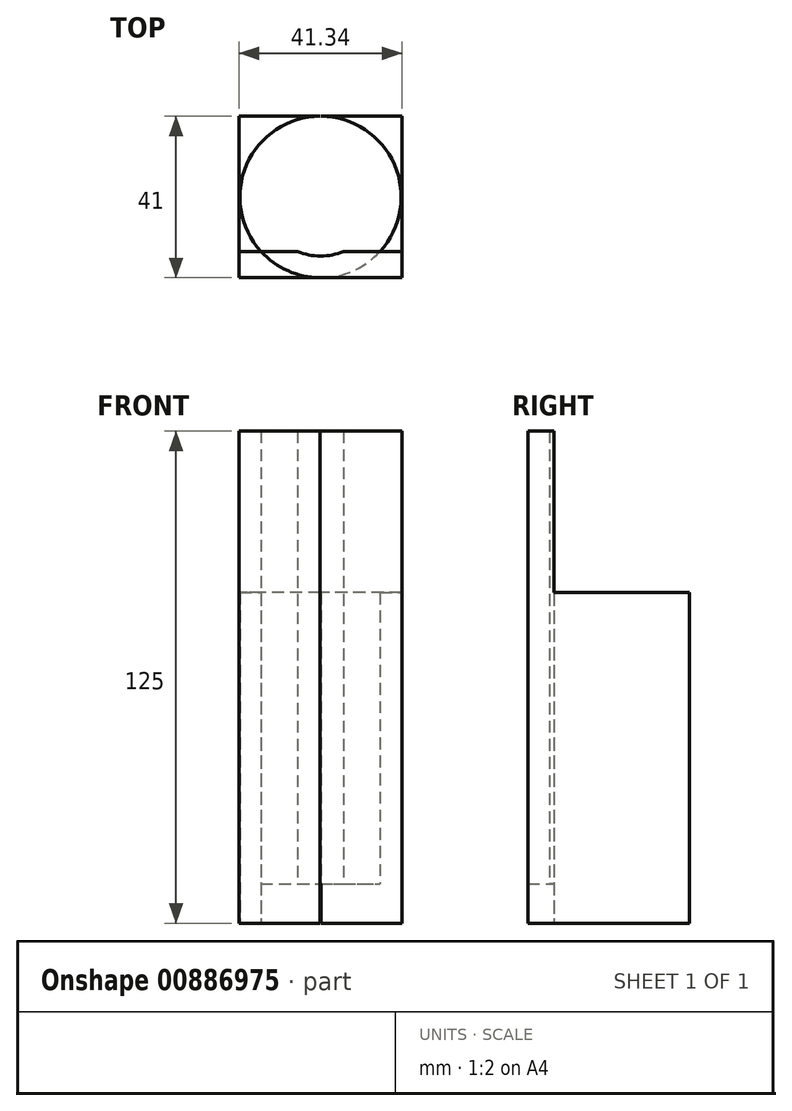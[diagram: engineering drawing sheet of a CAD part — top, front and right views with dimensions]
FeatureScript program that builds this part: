
annotation { "Feature Type Name" : "Feature", "Feature Type Description" : "" }
export const myFeature = defineFeature(function(context is Context, id is Id, definition is map)
    precondition{}
    {
        {
            var Q0;
            Q0=qCreatedBy(makeId("Top.planeOp"),FACE);
            var sketch = newSketch(context, id + "F0", { "sketchPlane" : qUnion([Q0])});
            skCircle(sketch, "E0", {"center": v(0, 0) * mm, "radius": 20.5 * mm});
            skLineSegment(sketch, "E1.bottom", {"start": v(20.67, 20.5) * mm, "end": v(-20.67, 20.5) * mm});
            skLineSegment(sketch, "E1.top", {"start": v(20.67, -20.5) * mm, "end": v(-20.67, -20.5) * mm});
            skLineSegment(sketch, "E1.left", {"start": v(20.67, 20.5) * mm, "end": v(20.67, -20.5) * mm});
            skLineSegment(sketch, "E1.right", {"start": v(-20.67, 20.5) * mm, "end": v(-20.67, -20.5) * mm});
            skLineSegment(sketch, "E2", {"start": v(-15.14, -13.82) * mm, "end": v(15.14, -13.82) * mm});
            skLineSegment(sketch, "E3", {"start": v(-15.14, -13.82) * mm, "end": v(-20.67, -13.82) * mm});
            skLineSegment(sketch, "E4", {"start": v(-20.67, -13.82) * mm, "end": v(20.95, -13.82) * mm});
            skCircle(sketch, "E5", {"center": v(0, 0) * mm, "radius": 15 * mm});
            skSolve(sketch);
        }
        {
            var Q0;
            {var subQ0=sQuery(id+"F0.wireOp",EDGE,"E1.bottom");var subQ1=sQuery(id+"F0.wireOp",EDGE,"E0");var subQ2=makeQuery(id+"F0.imprint","INTERSECT",VERTEX,{"disambiguationData":[OD(1.0)],"derivedFrom":[subQ1,subQ0]});Q0=makeQuery(id+"F0.imprint","IMPRINT",FACE,{"disambiguationData":[TD([[makeQuery(id+"F0.imprint","IMPRINT",EDGE,{"disambiguationData":[TD([[subQ2,1.0]])],"derivedFrom":subQ1}),-1.0]])]});}
            var Q1;
            {var subQ0=sQuery(id+"F0.wireOp",EDGE,"E1.bottom");var subQ1=sQuery(id+"F0.wireOp",EDGE,"E0");var subQ2=makeQuery(id+"F0.imprint","INTERSECT",VERTEX,{"disambiguationData":[OD(0.0)],"derivedFrom":[subQ1,subQ0]});Q1=makeQuery(id+"F0.imprint","IMPRINT",FACE,{"disambiguationData":[TD([[makeQuery(id+"F0.imprint","IMPRINT",EDGE,{"disambiguationData":[TD([[subQ2,-1.0]])],"derivedFrom":subQ1}),-1.0]])]});}
            extrude(context, id + "F1", {"entities" : qUnion([Q0, Q1]), "depth" : 84 * mm, "offsetDistance" : 25 * mm});
        }
        {
            var Q0;
            {var subQ0=sQuery(id+"F0.wireOp",EDGE,"E1.top");var subQ1=sQuery(id+"F0.wireOp",EDGE,"E0");var subQ2=makeQuery(id+"F0.imprint","INTERSECT",VERTEX,{"disambiguationData":[OD(0.0)],"derivedFrom":[subQ1,subQ0]});Q0=makeQuery(id+"F0.imprint","IMPRINT",FACE,{"disambiguationData":[TD([[makeQuery(id+"F0.imprint","IMPRINT",EDGE,{"disambiguationData":[TD([[subQ2,1.0]])],"derivedFrom":subQ1}),-1.0]])]});}
            var Q1;
            {var subQ0=sQuery(id+"F0.wireOp",EDGE,"E1.top");var subQ1=sQuery(id+"F0.wireOp",EDGE,"E0");var subQ2=makeQuery(id+"F0.imprint","INTERSECT",VERTEX,{"disambiguationData":[OD(1.0)],"derivedFrom":[subQ1,subQ0]});Q1=makeQuery(id+"F0.imprint","IMPRINT",FACE,{"disambiguationData":[TD([[makeQuery(id+"F0.imprint","IMPRINT",EDGE,{"disambiguationData":[TD([[subQ2,-1.0]])],"derivedFrom":subQ1}),-1.0]])]});}
            extrude(context, id + "F2", {"entities" : qUnion([Q0, Q1]), "depth" : 125 * mm, "offsetDistance" : 25 * mm});
        }
        {
            var Q0;
            {var subQ0=sQuery(id+"F0.wireOp",EDGE,"E1.top");var subQ1=sQuery(id+"F0.wireOp",EDGE,"E0");var subQ2=makeQuery(id+"F0.imprint","INTERSECT",VERTEX,{"disambiguationData":[OD(0.0)],"derivedFrom":[subQ1,subQ0]});Q0=makeQuery(id+"F0.imprint","IMPRINT",FACE,{"disambiguationData":[TD([[makeQuery(id+"F0.imprint","IMPRINT",EDGE,{"disambiguationData":[TD([[subQ2,1.0]])],"derivedFrom":subQ1}),1.0]])]});}
            extrude(context, id + "F3", {"entities" : qUnion([Q0]), "depth" : 115 * mm, "offsetDistance" : 25 * mm});
        }
        {
            var Q0;
            Q0=makeQuery(id+"F2.opExtrude","SWEPT_BODY",BODY,{"disambiguationData":[OSD([sQuery(id+"F0.wireOp",EDGE,"E0"),sQuery(id+"F0.wireOp",EDGE,"E1.top"),sQuery(id+"F0.wireOp",EDGE,"E1.left"),sQuery(id+"F0.wireOp",EDGE,"E4")])]});
            var Q1;
            Q1=makeQuery(id+"F2.opExtrude","SWEPT_BODY",BODY,{"disambiguationData":[OSD([sQuery(id+"F0.wireOp",EDGE,"E0"),sQuery(id+"F0.wireOp",EDGE,"E1.top"),sQuery(id+"F0.wireOp",EDGE,"E1.right"),sQuery(id+"F0.wireOp",EDGE,"E4")])]});
            var Q2;
            Q2=makeQuery(id+"F1.opExtrude","SWEPT_BODY",BODY,{"disambiguationData":[OSD([sQuery(id+"F0.wireOp",EDGE,"E0"),sQuery(id+"F0.wireOp",EDGE,"E1.bottom"),sQuery(id+"F0.wireOp",EDGE,"E1.right"),sQuery(id+"F0.wireOp",EDGE,"E4")])]});
            var Q3;
            Q3=makeQuery(id+"F1.opExtrude","SWEPT_BODY",BODY,{"disambiguationData":[OSD([sQuery(id+"F0.wireOp",EDGE,"E0"),sQuery(id+"F0.wireOp",EDGE,"E1.bottom"),sQuery(id+"F0.wireOp",EDGE,"E1.left"),sQuery(id+"F0.wireOp",EDGE,"E4")])]});
            transform(context, id + "F4", {"entities" : qUnion([Q0, Q1, Q2, Q3]), "transformType" : TransformType.TRANSLATION_3D, "dx" : 0 * mm, "dy" : 0 * mm, "dz" : -10 * mm, "makeCopy" : false});
        }
        {
            var Q0;
            {var subQ0=sQuery(id+"F0.wireOp",EDGE,"E1.bottom");var subQ1=sQuery(id+"F0.wireOp",EDGE,"E0");var subQ2=makeQuery(id+"F0.imprint","INTERSECT",VERTEX,{"disambiguationData":[OD(0.0)],"derivedFrom":[subQ1,subQ0]});Q0=makeQuery(id+"F0.imprint","IMPRINT",FACE,{"disambiguationData":[TD([[makeQuery(id+"F0.imprint","IMPRINT",EDGE,{"disambiguationData":[TD([[subQ2,1.0]])],"derivedFrom":subQ1}),1.0]])]});}
            extrude(context, id + "F5", {"entities" : qUnion([Q0]), "depth" : 74 * mm, "offsetDistance" : 25 * mm});
        }
        {
            var Q0;
            {var subQ0=sQuery(id+"F0.wireOp",EDGE,"E5");var subQ1=sQuery(id+"F0.wireOp",EDGE,"E4");var subQ2=makeQuery(id+"F0.imprint","INTERSECT",VERTEX,{"disambiguationData":[OD(0.0)],"derivedFrom":[subQ1,subQ0]});Q0=makeQuery(id+"F0.imprint","IMPRINT",FACE,{"disambiguationData":[TD([[makeQuery(id+"F0.imprint","IMPRINT",EDGE,{"disambiguationData":[TD([[subQ2,-1.0]])],"derivedFrom":subQ1}),-1.0]])]});}
            extrude(context, id + "F6", {"entities" : qUnion([Q0]), "operationType" : NewBodyOperationType.ADD, "depth" : 115 * mm, "offsetDistance" : 25 * mm});
        }
    });
